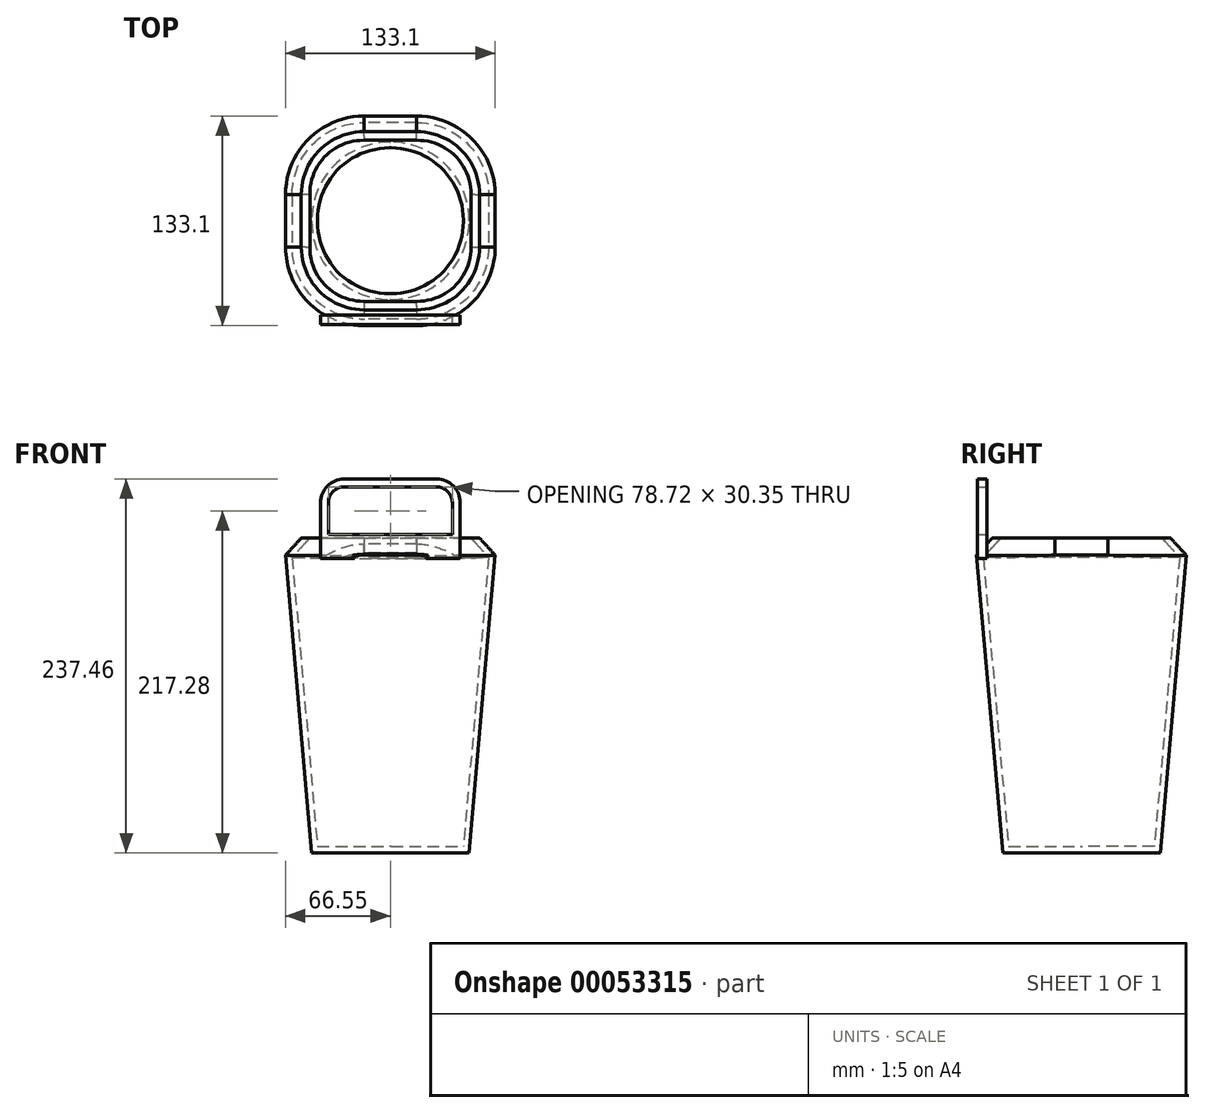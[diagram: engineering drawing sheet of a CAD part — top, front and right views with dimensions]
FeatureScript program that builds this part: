
annotation { "Feature Type Name" : "Feature", "Feature Type Description" : "" }
export const myFeature = defineFeature(function(context is Context, id is Id, definition is map)
    precondition{}
    {
        {
            var Q0;
            Q0=qCreatedBy(makeId("Top.planeOp"),FACE);
            var sketch = newSketch(context, id + "F0", { "sketchPlane" : qUnion([Q0])});
            skLineSegment(sketch, "E0.rect.bottom", {"start": v(-50, -50) * mm, "end": v(50, -50) * mm});
            skLineSegment(sketch, "E0.rect.top", {"start": v(-50, 50) * mm, "end": v(50, 50) * mm});
            skLineSegment(sketch, "E0.rect.left", {"start": v(-50, -50) * mm, "end": v(-50, 50) * mm});
            skLineSegment(sketch, "E0.rect.right", {"start": v(50, -50) * mm, "end": v(50, 50) * mm});
            skPoint(sketch, "E0.rect.middle", {"position": v(0, 0) * mm});
            skSolve(sketch);
        }
        {
            var Q0;
            Q0=makeQuery(id+"F0.imprint","IMPRINT",FACE,{"disambiguationData":[TD([[makeQuery(id+"F0.imprint","IMPRINT",EDGE,{"derivedFrom":sQuery(id+"F0.wireOp",EDGE,"E0.rect.bottom")}),1.0]])]});
            extrude(context, id + "F1", {"entities" : qUnion([Q0]), "depth" : 200 * mm, "hasDraft" : true, "draftAngle" : 5 * degree});
        }
        {
            var Q0;
            Q0=makeQuery(id+"F1.opExtrude","SWEPT_EDGE",EDGE,{"disambiguationData":[OSD([sQuery(id+"F0.wireOp",EDGE,"E0.rect.top"),sQuery(id+"F0.wireOp",EDGE,"E0.rect.left")])]});
            var Q1;
            Q1=makeQuery(id+"F1.opExtrude","SWEPT_EDGE",EDGE,{"disambiguationData":[OSD([sQuery(id+"F0.wireOp",EDGE,"E0.rect.bottom"),sQuery(id+"F0.wireOp",EDGE,"E0.rect.left")])]});
            var Q2;
            Q2=makeQuery(id+"F1.opExtrude","SWEPT_EDGE",EDGE,{"disambiguationData":[OSD([sQuery(id+"F0.wireOp",EDGE,"E0.rect.bottom"),sQuery(id+"F0.wireOp",EDGE,"E0.rect.right")])]});
            var Q3;
            Q3=makeQuery(id+"F1.opExtrude","SWEPT_EDGE",EDGE,{"disambiguationData":[OSD([sQuery(id+"F0.wireOp",EDGE,"E0.rect.top"),sQuery(id+"F0.wireOp",EDGE,"E0.rect.right")])]});
            fillet(context, id + "F2", {"entities" : qUnion([Q0, Q1, Q2, Q3]), "radius" : 50 * mm, "tangentPropagation" : true, "allowEdgeOverflow" : false});
        }
        {
            var Q0;
            Q0=makeQuery(id+"F1.opExtrude","CAP_FACE",FACE,{"disambiguationData":[OSD([sQuery(id+"F0.wireOp",EDGE,"E0.rect.bottom"),sQuery(id+"F0.wireOp",EDGE,"E0.rect.top"),sQuery(id+"F0.wireOp",EDGE,"E0.rect.left"),sQuery(id+"F0.wireOp",EDGE,"E0.rect.right")])],"isStart":false});
            chamfer(context, id + "F3", {"entities" : qUnion([Q0]), "width" : 10 * mm, "tangentPropagation" : true});
        }
        {
            var Q0;
            Q0=makeQuery(id+"F1.opExtrude","CAP_FACE",FACE,{"disambiguationData":[OSD([sQuery(id+"F0.wireOp",EDGE,"E0.rect.bottom"),sQuery(id+"F0.wireOp",EDGE,"E0.rect.top"),sQuery(id+"F0.wireOp",EDGE,"E0.rect.left"),sQuery(id+"F0.wireOp",EDGE,"E0.rect.right")])],"isStart":false});
            shell(context, id + "F4", {"entities" : qUnion([Q0]), "thickness" : 4 * mm});
        }
        {
            var Q0;
            Q0=qCreatedBy(makeId("Front.planeOp"),FACE);
            cPlane(context, id + "F5", {"entities" : qUnion([Q0]), "cplaneType" : CPlaneType.OFFSET, "offset" : 60 * mm, "width" : 150 * mm, "height" : 150 * mm});
        }
        {
            var Q0;
            Q0=qCreatedBy(id+"F5.planeOp",FACE);
            var sketch = newSketch(context, id + "F6", { "sketchPlane" : qUnion([Q0])});
            skLineSegment(sketch, "E1.rect.bottom", {"start": v(-44.36, 197.1) * mm, "end": v(44.36, 197.1) * mm});
            skLineSegment(sketch, "E1.rect.top", {"start": v(-29.36, 237.46) * mm, "end": v(29.36, 237.46) * mm});
            skLineSegment(sketch, "E1.rect.left", {"start": v(-44.36, 197.1) * mm, "end": v(-44.36, 222.46) * mm});
            skLineSegment(sketch, "E1.rect.right", {"start": v(44.36, 197.1) * mm, "end": v(44.36, 222.46) * mm});
            skPoint(sketch, "E1.rect.middle", {"position": v(0, 217.28) * mm});
            skPoint(sketch, "E2.visualSharp", {"position": v(44.36, 237.46) * mm});
            skArc(sketch, "E2.filletArc", {"start": v(44.36, 222.46) * mm, "mid": v(39.96, 233.06) * mm, "end": v(29.36, 237.46) * mm});
            skPoint(sketch, "E3.visualSharp", {"position": v(-44.36, 237.46) * mm});
            skArc(sketch, "E3.filletArc", {"start": v(-29.36, 237.46) * mm, "mid": v(-39.96, 233.06) * mm, "end": v(-44.36, 222.46) * mm});
            skArc(sketch, "E4.0", {"start": v(-29.36, 232.46) * mm, "mid": v(-36.43, 229.53) * mm, "end": v(-39.36, 222.46) * mm});
            skArc(sketch, "E4.1", {"start": v(39.36, 222.46) * mm, "mid": v(36.43, 229.53) * mm, "end": v(29.36, 232.46) * mm});
            skLineSegment(sketch, "E4.2", {"start": v(39.36, 202.1) * mm, "end": v(39.36, 222.46) * mm});
            skLineSegment(sketch, "E4.3", {"start": v(-29.36, 232.46) * mm, "end": v(29.36, 232.46) * mm});
            skLineSegment(sketch, "E4.4", {"start": v(-39.36, 202.1) * mm, "end": v(39.36, 202.1) * mm});
            skLineSegment(sketch, "E4.5", {"start": v(-39.36, 202.1) * mm, "end": v(-39.36, 222.46) * mm});
            skSolve(sketch);
        }
        {
            var Q0;
            Q0=makeQuery(id+"F6.imprint","IMPRINT",FACE,{"disambiguationData":[TD([[makeQuery(id+"F6.imprint","IMPRINT",EDGE,{"derivedFrom":sQuery(id+"F6.wireOp",EDGE,"E1.rect.bottom")}),1.0]])]});
            extrude(context, id + "F7", {"entities" : qUnion([Q0]), "operationType" : NewBodyOperationType.ADD, "depth" : 6 * mm});
        }
        {
            var Q0;
            Q0=makeQuery(id+"F7.opExtrude","SWEPT_FACE",FACE,{"disambiguationData":[OSD([sQuery(id+"F6.wireOp",EDGE,"E1.rect.bottom")])]});
            extrude(context, id + "F8", {"entities" : qUnion([Q0]), "operationType" : NewBodyOperationType.ADD, "depth" : 10 * mm});
        }
    });
